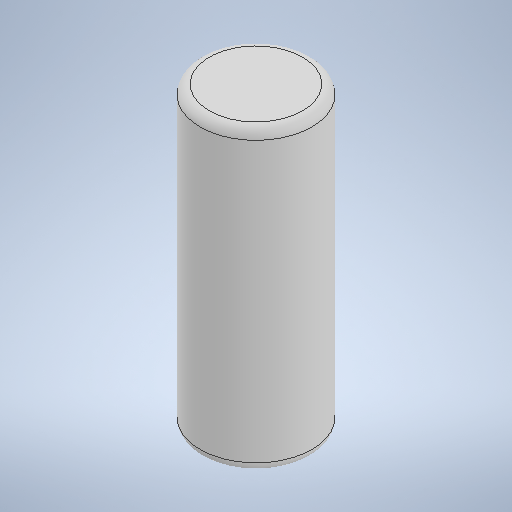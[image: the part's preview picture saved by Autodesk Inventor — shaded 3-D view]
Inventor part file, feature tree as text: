
AUTODESK INVENTOR PART (.ipt)
format: ipt  version: 2025.1 (Build 291241000, 241)  size: 236,544 bytes
history: native  units: mm
features: extrude x1, fillet x1, sketch x1
ambient origin geometry x8: Origin, YZ Plane, XZ Plane, XY Plane, X Axis, Y Axis, Z Axis, Center Point
bodies: Solid1 (feature_tree)
feature tree (3):
  extrude  "Extrusion1"  Depth=8.0mm TaperAngle=0.0deg
  fillet  "Fillet1"  Radius=0.25mm
  sketch  "Sketch1"  dims[d0=3.0mm d1=8.0mm d2=0.0mm d3=0.25mm]
